# Revit family: ledlinear-fiji_l600_12w-830_840-bl_521028002800_06c9
name_source: partatom
category: Lighting Fixtures
units: mm (PartAtom-declared; Revit-internal decimal feet)

## family parameters
Cut with Voids When Loaded = No
Host = Face
Light Source = No
Part Type = Normal
Room Calculation Point = No
Round Connector Dimension = Use Diameter
Shared = No

## types (1)
- LEDLinear-Fiji L600 12W-830/840-BL (1 x LED, 1560 lm, 4000)
    Apparent Load = 12 VA
    Approval mark = CE
    CIE Flux Codes = 40 69 88 80 100
    Color Rendering = 80
    Color Temperature = 4000
    Control Gear = Electronic ballast
    Default Elevation = 1800 mm
    Description = Mirror Light 600mm-12W-1560lm-3/4000K-160°x110°-IP44
    Frequency = 60 Hz
    Height = 46 mm
    Lamp = 1 x LED
    Lamp Light Flux = 1560 lm
    Lamp count = 1
    Length = 600 mm
    Luminous efficacy = 130 lm/W
    Manufacturer = OPPLE
    ModVariant = No
    Model = 521028002800
    Number of Poles = 1
    OnlyDefault = Yes
    Power Factor = 1
    Product Name = LEDLinear-Fiji L600 12W-830/840-BL
    Product group = Ceiling / wall-mounted luminaires
    ProductGroupID = 30
    Protection Class = Protection class I
    Protection Degree = IP 44
    RLX_Detail_Level = 1
    RLX_Emergency_Light_Flux = 0 lm
    RLX_Emergency_Type = 0
    RLX_Emergency_Type_DB = No
    RlxData = <blob elided: 163313 chars, md5=d321349d>
    Socket = socket
    Standby Power = 0 W
    System Light Flux = 1560 lm
    System Power = 12 W
    Type Comments = Product without accessories
    Type Image = web_lin_mirror_fiji.jpg
    URL = http://relux.com
    VarID = ---
    Voltage = 230 V
    Voltage Range = 220-240 V
    Weight = 0.00 kg
    Width = 72 mm  [stored 0.23622 ft]

note: [stored X ft] marks values corroborated as IEEE doubles in the binary element streams (Revit-internal decimal feet)

## geometry (parser evidence)
native form markers: Blend x4, Sweep x11
no freeform markers — native parametric forms only
